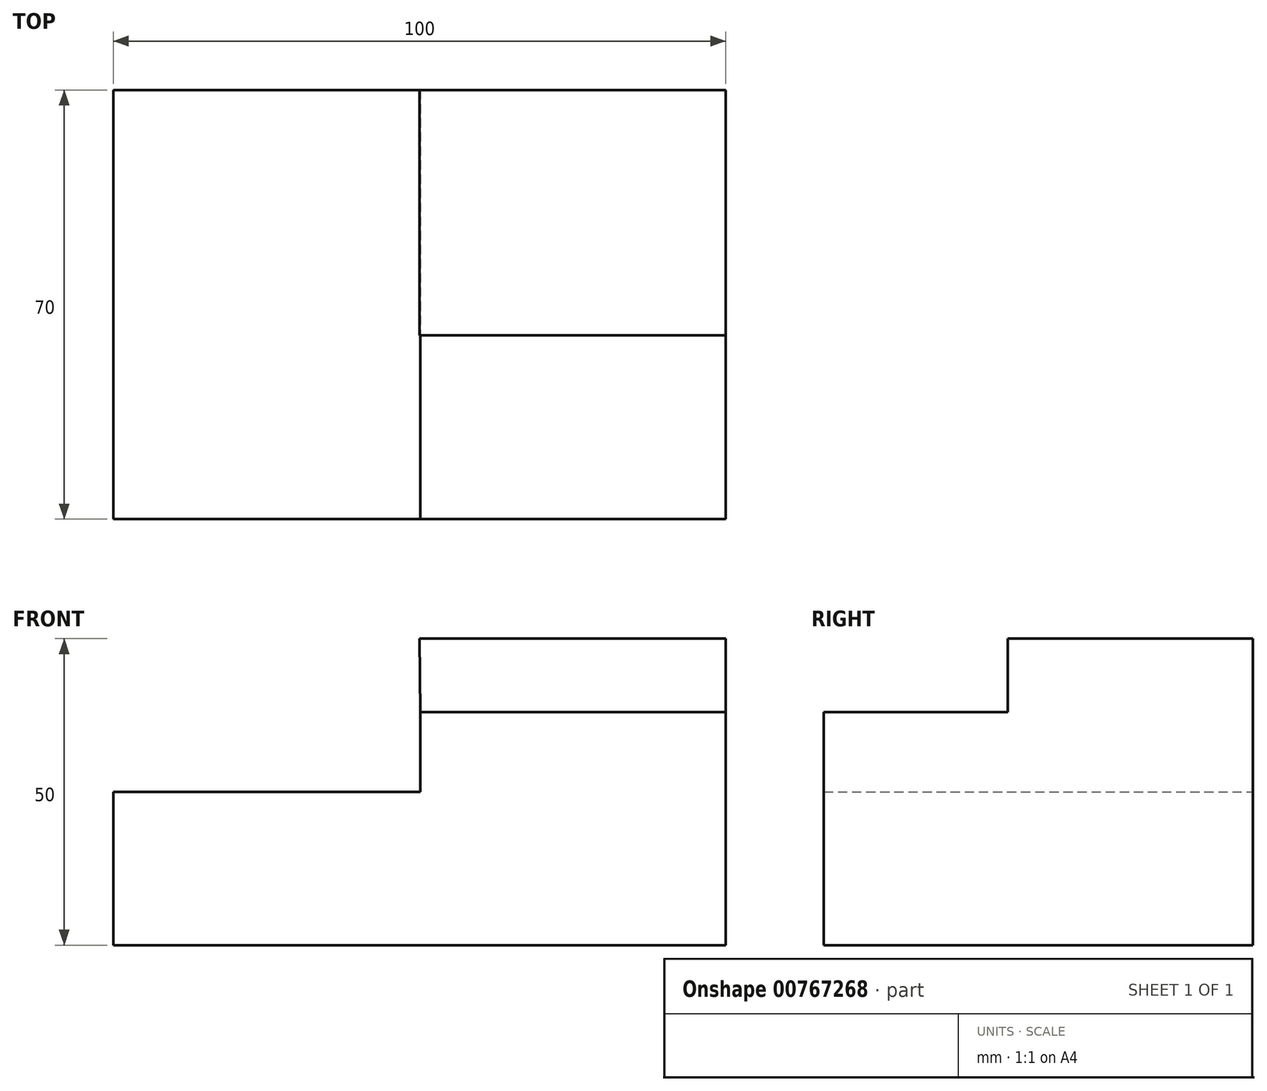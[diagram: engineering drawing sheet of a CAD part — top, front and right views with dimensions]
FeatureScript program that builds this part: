
annotation { "Feature Type Name" : "Feature", "Feature Type Description" : "" }
export const myFeature = defineFeature(function(context is Context, id is Id, definition is map)
    precondition{}
    {
        {
            var Q0;
            Q0=qCreatedBy(makeId("Front.planeOp"),FACE);
            var sketch = newSketch(context, id + "F0", { "sketchPlane" : qUnion([Q0])});
            skLineSegment(sketch, "E0", {"start": v(-50.1, -53.1) * mm, "end": v(49.9, -53.1) * mm});
            skLineSegment(sketch, "E1", {"start": v(49.9, -53.1) * mm, "end": v(49.9, -3.1) * mm});
            skLineSegment(sketch, "E2", {"start": v(49.9, -3.1) * mm, "end": v(-0.1, -3.1) * mm});
            skLineSegment(sketch, "E3", {"start": v(-0.1, -3.1) * mm, "end": v(0, -15.1) * mm});
            skLineSegment(sketch, "E4", {"start": v(0, -15.1) * mm, "end": v(49.9, -15.1) * mm});
            skLineSegment(sketch, "E5", {"start": v(-50.1, -53.1) * mm, "end": v(-50.1, -28.1) * mm});
            skLineSegment(sketch, "E6", {"start": v(-50.1, -28.1) * mm, "end": v(0, -28.1) * mm});
            skLineSegment(sketch, "E7", {"start": v(0, -28.1) * mm, "end": v(0, -15.1) * mm});
            skSolve(sketch);
        }
        {
            var Q0;
            {var subQ1=sQuery(id+"F0.wireOp",EDGE,"E0");Q0=makeQuery(id+"F0.imprint","IMPRINT",FACE,{"disambiguationData":[TD([[makeQuery(id+"F0.imprint","IMPRINT",EDGE,{"derivedFrom":subQ1}),1.0]])]});}
            extrude(context, id + "F1", {"entities" : qUnion([Q0]), "depth" : 30 * mm, "offsetDistance" : 25 * mm});
        }
        {
            var Q0;
            {var subQ0=sQuery(id+"F0.wireOp",EDGE,"E2");Q0=makeQuery(id+"F0.imprint","IMPRINT",FACE,{"disambiguationData":[TD([[makeQuery(id+"F0.imprint","IMPRINT",EDGE,{"derivedFrom":subQ0}),1.0]])]});}
            extrude(context, id + "F2", {"entities" : qUnion([Q0]), "operationType" : NewBodyOperationType.ADD, "oppositeDirection" : true, "depth" : 40 * mm, "offsetDistance" : 25 * mm});
        }
        {
            var Q0;
            {var subQ1=sQuery(id+"F0.wireOp",EDGE,"E0");Q0=makeQuery(id+"F0.imprint","IMPRINT",FACE,{"disambiguationData":[TD([[makeQuery(id+"F0.imprint","IMPRINT",EDGE,{"derivedFrom":subQ1}),1.0]])]});}
            extrude(context, id + "F3", {"entities" : qUnion([Q0]), "operationType" : NewBodyOperationType.ADD, "oppositeDirection" : true, "depth" : 40 * mm, "offsetDistance" : 25 * mm});
        }
    });
